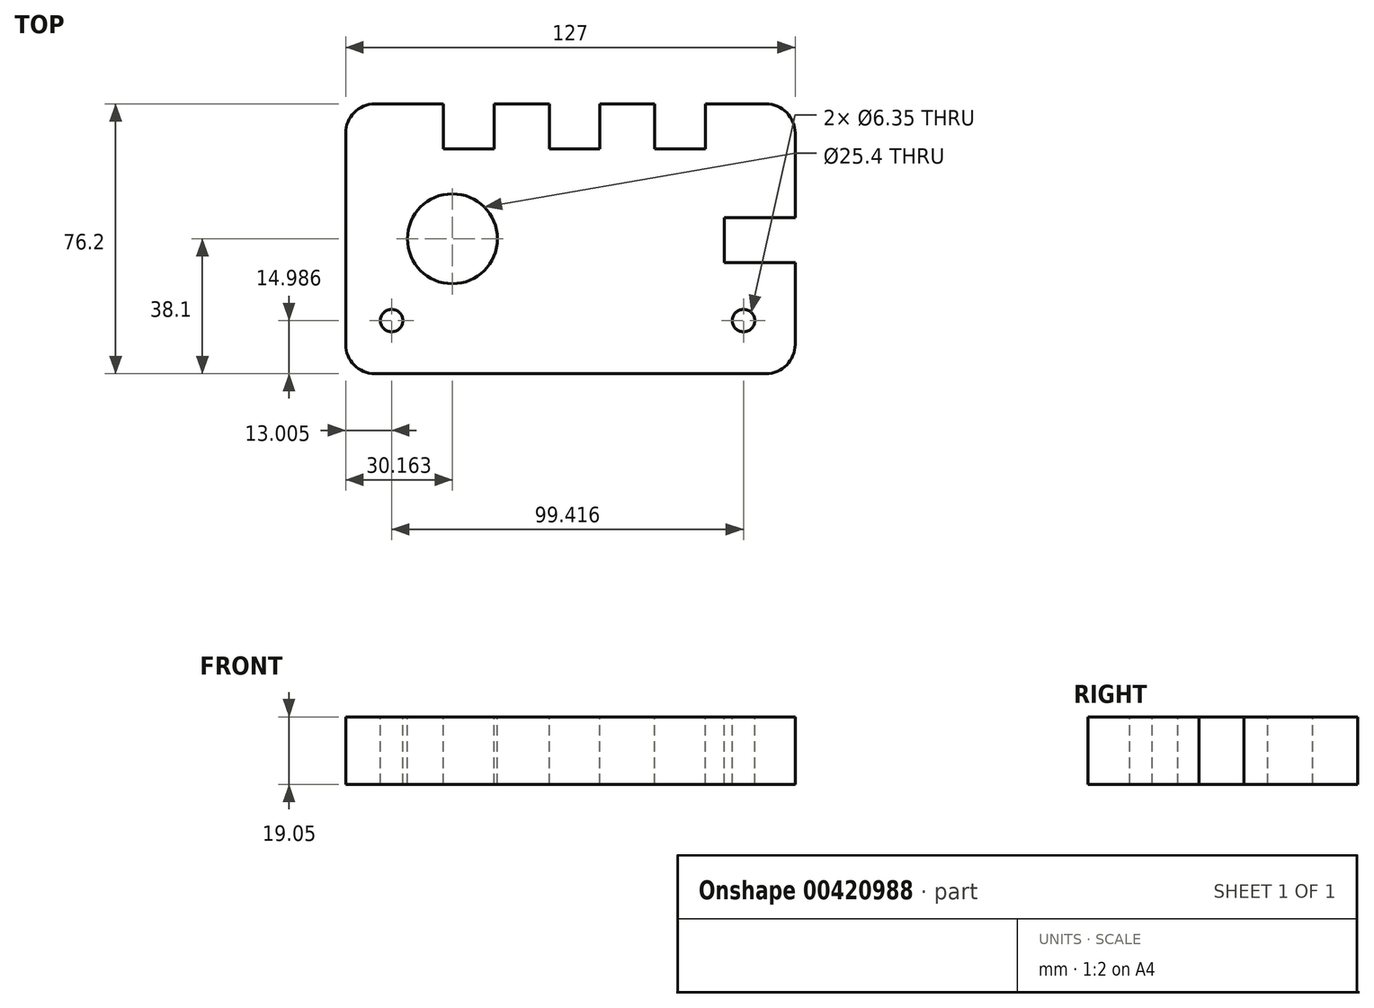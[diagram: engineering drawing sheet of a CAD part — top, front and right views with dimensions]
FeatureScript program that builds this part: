
annotation { "Feature Type Name" : "Feature", "Feature Type Description" : "" }
export const myFeature = defineFeature(function(context is Context, id is Id, definition is map)
    precondition{}
    {
        {
            var Q0;
            Q0=qCreatedBy(makeId("Top.planeOp"),FACE);
            var sketch = newSketch(context, id + "F0", { "sketchPlane" : qUnion([Q0])});
            skLineSegment(sketch, "E0.bottom", {"start": v(8.25, 0) * mm, "end": v(118.75, 0) * mm});
            skLineSegment(sketch, "E0.top", {"start": v(8.25, 76.2) * mm, "end": v(118.75, 76.2) * mm});
            skLineSegment(sketch, "E0.left", {"start": v(0, 8.26) * mm, "end": v(0, 67.95) * mm});
            skLineSegment(sketch, "E0.right", {"start": v(127, 8.26) * mm, "end": v(127, 67.95) * mm});
            skPoint(sketch, "E1.visualSharp", {"position": v(0, 76.2) * mm});
            skArc(sketch, "E1.filletArc", {"start": v(8.25, 76.2) * mm, "mid": v(2.42, 73.78) * mm, "end": v(0, 67.95) * mm});
            skPoint(sketch, "E2.visualSharp", {"position": v(127, 76.2) * mm});
            skArc(sketch, "E2.filletArc", {"start": v(127, 67.95) * mm, "mid": v(124.58, 73.78) * mm, "end": v(118.75, 76.2) * mm});
            skPoint(sketch, "E3.visualSharp", {"position": v(127, 0) * mm});
            skArc(sketch, "E3.filletArc", {"start": v(118.75, 0) * mm, "mid": v(124.58, 2.42) * mm, "end": v(127, 8.26) * mm});
            skPoint(sketch, "E4.visualSharp", {"position": v(0, 0) * mm});
            skArc(sketch, "E4.filletArc", {"start": v(0, 8.26) * mm, "mid": v(2.42, 2.42) * mm, "end": v(8.25, 0) * mm});
            skSolve(sketch);
        }
        {
            var Q0;
            Q0 = qSketchRegion(id + "F0", true);
            extrude(context, id + "F1", {"entities" : qUnion([Q0]), "depth" : 19.05 * mm});
        }
        {
            var Q0;
            Q0=makeQuery(id+"F1.opExtrude","CAP_FACE",FACE,{"disambiguationData":[OSD([sQuery(id+"F0.wireOp",EDGE,"E0.bottom"),sQuery(id+"F0.wireOp",EDGE,"E0.top"),sQuery(id+"F0.wireOp",EDGE,"E0.left"),sQuery(id+"F0.wireOp",EDGE,"E0.right"),sQuery(id+"F0.wireOp",EDGE,"E1.filletArc"),sQuery(id+"F0.wireOp",EDGE,"E2.filletArc"),sQuery(id+"F0.wireOp",EDGE,"E3.filletArc"),sQuery(id+"F0.wireOp",EDGE,"E4.filletArc")])],"isStart":false});
            var sketch = newSketch(context, id + "F2", { "sketchPlane" : qUnion([Q0])});
            skLineSegment(sketch, "E5", {"start": v(127, 44.07) * mm, "end": v(106.98, 44.07) * mm});
            skLineSegment(sketch, "E6.MirrorCS", {"start": v(127, 31.37) * mm, "end": v(106.98, 31.37) * mm});
            skLineSegment(sketch, "E7", {"start": v(106.98, 44.07) * mm, "end": v(106.98, 31.37) * mm});
            skLineSegment(sketch, "E8", {"start": v(127, 67.95) * mm, "end": v(127, 79.24) * mm, "construction": true});
            skLineSegment(sketch, "E9", {"start": v(118.75, 76.2) * mm, "end": v(119.26, 76.2) * mm, "construction": true});
            skLineSegment(sketch, "E10", {"start": v(127, 76.2) * mm, "end": v(101.6, 76.2) * mm, "construction": true});
            skLineSegment(sketch, "E11.bottom", {"start": v(101.6, 76.2) * mm, "end": v(87.31, 76.2) * mm});
            skLineSegment(sketch, "E11.top", {"start": v(101.6, 63.5) * mm, "end": v(87.31, 63.5) * mm});
            skLineSegment(sketch, "E11.left", {"start": v(101.6, 76.2) * mm, "end": v(101.6, 63.5) * mm});
            skLineSegment(sketch, "E11.right", {"start": v(87.31, 76.2) * mm, "end": v(87.31, 63.5) * mm});
            skLineSegment(sketch, "E12", {"start": v(71.84, 76.2) * mm, "end": v(71.84, 63.5) * mm});
            skLineSegment(sketch, "E13", {"start": v(71.84, 63.5) * mm, "end": v(57.56, 63.5) * mm});
            skLineSegment(sketch, "E14", {"start": v(57.56, 63.5) * mm, "end": v(57.56, 76.2) * mm});
            skLineSegment(sketch, "E15", {"start": v(57.56, 76.2) * mm, "end": v(71.84, 76.2) * mm});
            skLineSegment(sketch, "E16.bottom", {"start": v(41.94, 76.2) * mm, "end": v(27.65, 76.2) * mm});
            skLineSegment(sketch, "E16.top", {"start": v(41.94, 63.5) * mm, "end": v(27.65, 63.5) * mm});
            skLineSegment(sketch, "E16.left", {"start": v(41.94, 76.2) * mm, "end": v(41.94, 63.5) * mm});
            skLineSegment(sketch, "E16.right", {"start": v(27.65, 76.2) * mm, "end": v(27.65, 63.5) * mm});
            skLineSegment(sketch, "E17", {"start": v(30.16, 0) * mm, "end": v(30.16, 38.1) * mm, "construction": true});
            skCircle(sketch, "E18", {"center": v(30.16, 38.1) * mm, "radius": 12.7 * mm});
            skLineSegment(sketch, "E19", {"start": v(127, 14.99) * mm, "end": v(112.42, 14.99) * mm, "construction": true});
            skLineSegment(sketch, "E20", {"start": v(0, 14.99) * mm, "end": v(13, 14.99) * mm, "construction": true});
            skCircle(sketch, "E21", {"center": v(13, 14.99) * mm, "radius": 3.18 * mm});
            skCircle(sketch, "E22", {"center": v(112.42, 14.99) * mm, "radius": 3.18 * mm});
            skSolve(sketch);
        }
        {
            var Q0;
            Q0 = qSketchRegion(id + "F2", true);
            var Q1;
            {var subQ0=sQuery(id+"F2.wireOp",EDGE,"E5");Q1=makeQuery(id+"F2.imprint","IMPRINT",FACE,{"disambiguationData":[TD([[makeQuery(id+"F2.imprint","IMPRINT",EDGE,{"derivedFrom":subQ0}),1.0]])]});}
            extrude(context, id + "F3", {"entities" : qUnion([Q0, Q1]), "operationType" : NewBodyOperationType.REMOVE, "endBound" : BoundingType.THROUGH_ALL, "oppositeDirection" : true, "depth" : 25.4 * mm});
        }
    });
